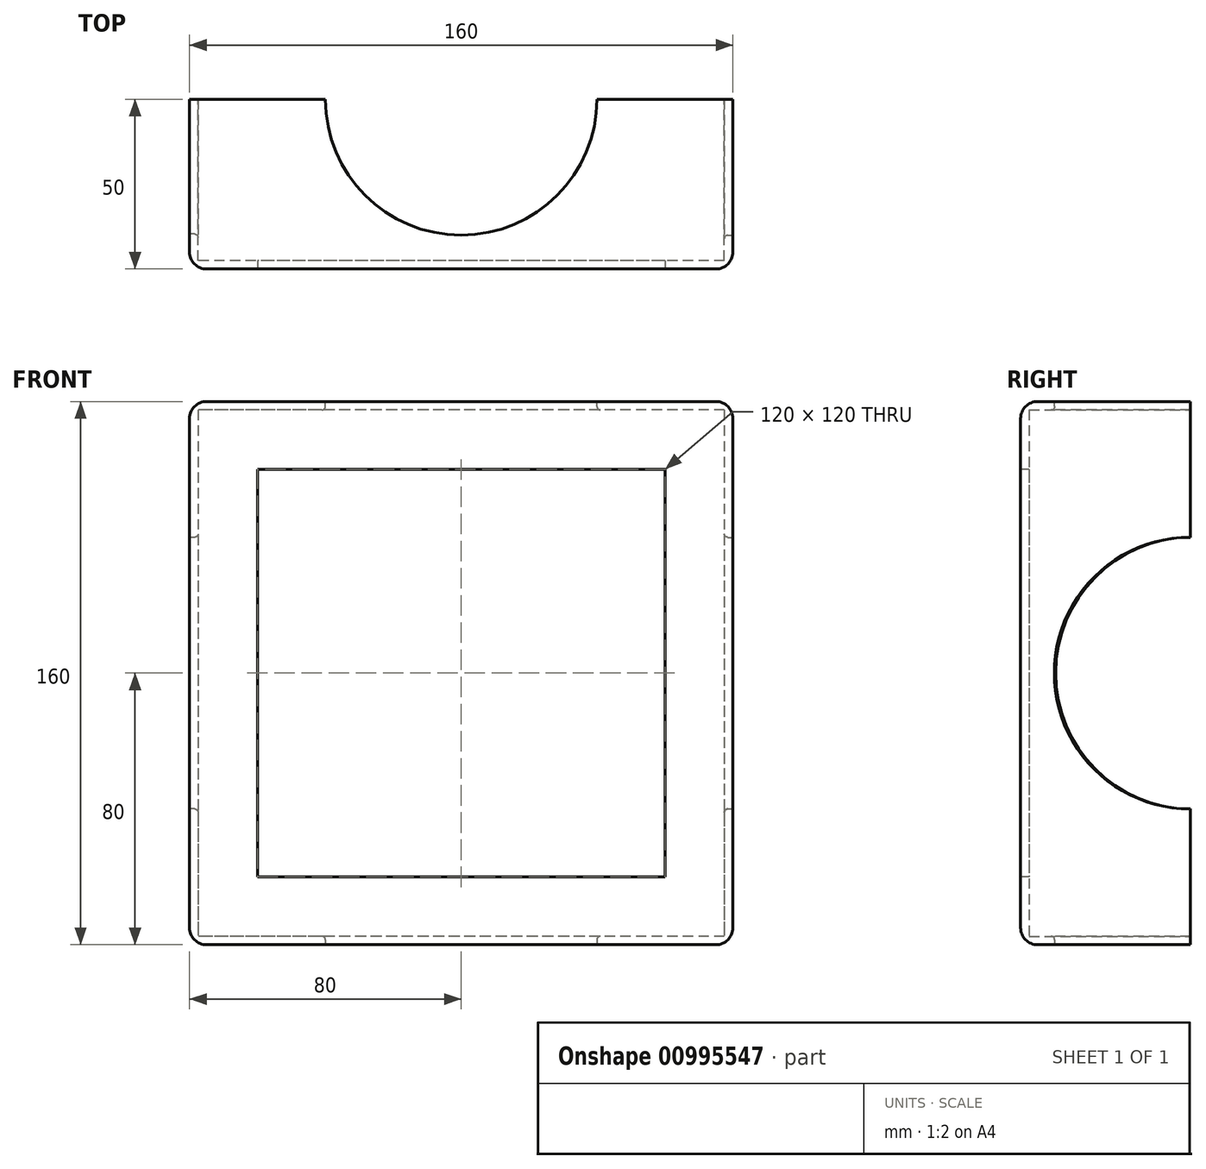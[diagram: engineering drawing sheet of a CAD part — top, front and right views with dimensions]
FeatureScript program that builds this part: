
annotation { "Feature Type Name" : "Feature", "Feature Type Description" : "" }
export const myFeature = defineFeature(function(context is Context, id is Id, definition is map)
    precondition{}
    {
        {
            var Q0;
            Q0=qCreatedBy(makeId("Front.planeOp"),FACE);
            var sketch = newSketch(context, id + "F0", { "sketchPlane" : qUnion([Q0])});
            skLineSegment(sketch, "E0.bottom", {"start": v(80, 80) * mm, "end": v(-80, 80) * mm});
            skLineSegment(sketch, "E0.top", {"start": v(80, -80) * mm, "end": v(-80, -80) * mm});
            skLineSegment(sketch, "E0.left", {"start": v(80, 80) * mm, "end": v(80, -80) * mm});
            skLineSegment(sketch, "E0.right", {"start": v(-80, 80) * mm, "end": v(-80, -80) * mm});
            skPoint(sketch, "E0.middle", {"position": v(0, 0) * mm});
            skSolve(sketch);
        }
        {
            var Q0;
            Q0 = qSketchRegion(id + "F0", true);
            extrude(context, id + "F1", {"entities" : qUnion([Q0]), "depth" : 50 * mm, "offsetDistance" : 25 * mm});
        }
        {
            var Q0;
            Q0=makeQuery(id+"F1.opExtrude","CAP_FACE",FACE,{"disambiguationData":[OSD([sQuery(id+"F0.wireOp",EDGE,"E0.bottom"),sQuery(id+"F0.wireOp",EDGE,"E0.top"),sQuery(id+"F0.wireOp",EDGE,"E0.left"),sQuery(id+"F0.wireOp",EDGE,"E0.right")])],"isStart":true});
            shell(context, id + "F2", {"entities" : qUnion([Q0]), "thickness" : 2.5 * mm});
        }
        {
            var Q0;
            Q0=makeQuery(id+"F1.opExtrude","SWEPT_FACE",FACE,{"disambiguationData":[OSD([sQuery(id+"F0.wireOp",EDGE,"E0.top")])]});
            var sketch = newSketch(context, id + "F3", { "sketchPlane" : qUnion([Q0])});
            skArc(sketch, "E1", {"start": v(40, 0) * mm, "mid": v(0, 40) * mm, "end": v(-40, 0) * mm});
            skSolve(sketch);
        }
        {
            var Q0;
            {var subQ0=sQuery(id+"F3.wireOp",EDGE,"E1");Q0=makeQuery(id+"F3.imprint","IMPRINT",FACE,{"disambiguationData":[TD([[makeQuery(id+"F3.imprint","IMPRINT",EDGE,{"derivedFrom":subQ0}),1.0]])]});}
            extrude(context, id + "F4", {"entities" : qUnion([Q0]), "operationType" : NewBodyOperationType.REMOVE, "oppositeDirection" : true, "depth" : 25 * mm, "offsetDistance" : 25 * mm});
        }
        {
            var Q0;
            Q0=makeQuery(id+"F1.opExtrude","SWEPT_FACE",FACE,{"disambiguationData":[OSD([sQuery(id+"F0.wireOp",EDGE,"E0.right")])]});
            var sketch = newSketch(context, id + "F5", { "sketchPlane" : qUnion([Q0])});
            skArc(sketch, "E2", {"start": v(0, -40) * mm, "mid": v(39.7, 0) * mm, "end": v(0, 40) * mm});
            skSolve(sketch);
        }
        {
            var Q0;
            {var subQ0=sQuery(id+"F5.wireOp",EDGE,"E2");Q0=makeQuery(id+"F5.imprint","IMPRINT",FACE,{"disambiguationData":[TD([[makeQuery(id+"F5.imprint","IMPRINT",EDGE,{"derivedFrom":subQ0}),1.0]])]});}
            extrude(context, id + "F6", {"entities" : qUnion([Q0]), "operationType" : NewBodyOperationType.REMOVE, "oppositeDirection" : true, "depth" : 25 * mm, "offsetDistance" : 25 * mm});
        }
        {
            var Q0;
            Q0=makeQuery(id+"F1.opExtrude","SWEPT_FACE",FACE,{"disambiguationData":[OSD([sQuery(id+"F0.wireOp",EDGE,"E0.bottom")])]});
            var sketch = newSketch(context, id + "F7", { "sketchPlane" : qUnion([Q0])});
            skArc(sketch, "E3", {"start": v(-40, 0) * mm, "mid": v(0, -40) * mm, "end": v(40, 0) * mm});
            skSolve(sketch);
        }
        {
            var Q0;
            {var subQ0=sQuery(id+"F7.wireOp",EDGE,"E3");Q0=makeQuery(id+"F7.imprint","IMPRINT",FACE,{"disambiguationData":[TD([[makeQuery(id+"F7.imprint","IMPRINT",EDGE,{"derivedFrom":subQ0}),1.0]])]});}
            extrude(context, id + "F8", {"entities" : qUnion([Q0]), "operationType" : NewBodyOperationType.REMOVE, "oppositeDirection" : true, "depth" : 25 * mm, "offsetDistance" : 25 * mm});
        }
        {
            var Q0;
            Q0=makeQuery(id+"F1.opExtrude","SWEPT_FACE",FACE,{"disambiguationData":[OSD([sQuery(id+"F0.wireOp",EDGE,"E0.left")])]});
            var sketch = newSketch(context, id + "F9", { "sketchPlane" : qUnion([Q0])});
            skArc(sketch, "E4", {"start": v(0, 40) * mm, "mid": v(-40.08, 0) * mm, "end": v(0, -40) * mm});
            skSolve(sketch);
        }
        {
            var Q0;
            {var subQ0=sQuery(id+"F9.wireOp",EDGE,"E4");Q0=makeQuery(id+"F9.imprint","IMPRINT",FACE,{"disambiguationData":[TD([[makeQuery(id+"F9.imprint","IMPRINT",EDGE,{"derivedFrom":subQ0}),1.0]])]});}
            extrude(context, id + "F10", {"entities" : qUnion([Q0]), "operationType" : NewBodyOperationType.REMOVE, "oppositeDirection" : true, "depth" : 25 * mm, "offsetDistance" : 25 * mm});
        }
        {
            var Q0;
            Q0=makeQuery(id+"F1.opExtrude","CAP_FACE",FACE,{"disambiguationData":[OSD([sQuery(id+"F0.wireOp",EDGE,"E0.bottom"),sQuery(id+"F0.wireOp",EDGE,"E0.top"),sQuery(id+"F0.wireOp",EDGE,"E0.left"),sQuery(id+"F0.wireOp",EDGE,"E0.right")])],"isStart":false});
            var sketch = newSketch(context, id + "F11", { "sketchPlane" : qUnion([Q0])});
            skLineSegment(sketch, "E5.bottom", {"start": v(60, 60) * mm, "end": v(-60, 60) * mm});
            skLineSegment(sketch, "E5.top", {"start": v(60, -60) * mm, "end": v(-60, -60) * mm});
            skLineSegment(sketch, "E5.left", {"start": v(60, 60) * mm, "end": v(60, -60) * mm});
            skLineSegment(sketch, "E5.right", {"start": v(-60, 60) * mm, "end": v(-60, -60) * mm});
            skPoint(sketch, "E5.middle", {"position": v(0, 0) * mm});
            skSolve(sketch);
        }
        {
            var Q0;
            Q0=makeQuery(id+"F11.imprint","IMPRINT",FACE,{"disambiguationData":[TD([[makeQuery(id+"F11.imprint","IMPRINT",EDGE,{"derivedFrom":sQuery(id+"F11.wireOp",EDGE,"E5.bottom")}),1.0]])]});
            extrude(context, id + "F12", {"entities" : qUnion([Q0]), "operationType" : NewBodyOperationType.REMOVE, "oppositeDirection" : true, "depth" : 25 * mm, "offsetDistance" : 25 * mm});
        }
        {
            var Q0;
            Q0=makeQuery(id+"F1.opExtrude","SWEPT_EDGE",EDGE,{"disambiguationData":[OSD([sQuery(id+"F0.wireOp",EDGE,"E0.bottom"),sQuery(id+"F0.wireOp",EDGE,"E0.left")])]});
            var Q1;
            Q1=makeQuery(id+"F1.opExtrude","CAP_EDGE",EDGE,{"disambiguationData":[OSD([sQuery(id+"F0.wireOp",EDGE,"E0.bottom")])],"isStart":false});
            var Q2;
            Q2=makeQuery(id+"F1.opExtrude","CAP_EDGE",EDGE,{"disambiguationData":[OSD([sQuery(id+"F0.wireOp",EDGE,"E0.left")])],"isStart":false});
            var Q3;
            Q3=makeQuery(id+"F1.opExtrude","SWEPT_EDGE",EDGE,{"disambiguationData":[OSD([sQuery(id+"F0.wireOp",EDGE,"E0.top"),sQuery(id+"F0.wireOp",EDGE,"E0.left")])]});
            var Q4;
            Q4=makeQuery(id+"F1.opExtrude","CAP_EDGE",EDGE,{"disambiguationData":[OSD([sQuery(id+"F0.wireOp",EDGE,"E0.top")])],"isStart":false});
            var Q5;
            Q5=makeQuery(id+"F1.opExtrude","SWEPT_EDGE",EDGE,{"disambiguationData":[OSD([sQuery(id+"F0.wireOp",EDGE,"E0.top"),sQuery(id+"F0.wireOp",EDGE,"E0.right")])]});
            var Q6;
            Q6=makeQuery(id+"F1.opExtrude","CAP_EDGE",EDGE,{"disambiguationData":[OSD([sQuery(id+"F0.wireOp",EDGE,"E0.right")])],"isStart":false});
            var Q7;
            Q7=makeQuery(id+"F1.opExtrude","SWEPT_EDGE",EDGE,{"disambiguationData":[OSD([sQuery(id+"F0.wireOp",EDGE,"E0.bottom"),sQuery(id+"F0.wireOp",EDGE,"E0.right")])]});
            fillet(context, id + "F13", {"entities" : qUnion([Q0, Q1, Q2, Q3, Q4, Q5, Q6, Q7]), "radius" : 5 * mm, "tangentPropagation" : true, "allowEdgeOverflow" : false});
        }
        {
            var Q0;
            Q0=makeQuery(id+"F4.boolean.opBoolean","INTERSECT",EDGE,{"derivedFrom":[makeQuery(id+"F2.opShell","OFFSET_FACE",FACE,{"disambiguationData":[OSD([sQuery(id+"F0.wireOp",EDGE,"E0.top")])]}),makeQuery(id+"F4.opExtrude","SWEPT_FACE",FACE,{"disambiguationData":[OSD([sQuery(id+"F3.wireOp",EDGE,"E1")])]})]});
            var Q1;
            Q1=makeQuery(id+"F4.boolean.opBoolean","COPY",EDGE,{"derivedFrom":makeQuery(id+"F4.opExtrude","CAP_EDGE",EDGE,{"disambiguationData":[OSD([sQuery(id+"F3.wireOp",EDGE,"E1")])],"isStart":true})});
            var Q2;
            Q2=makeQuery(id+"F10.boolean.opBoolean","INTERSECT",EDGE,{"derivedFrom":[makeQuery(id+"F2.opShell","OFFSET_FACE",FACE,{"disambiguationData":[OSD([sQuery(id+"F0.wireOp",EDGE,"E0.left")])]}),makeQuery(id+"F10.opExtrude","SWEPT_FACE",FACE,{"disambiguationData":[OSD([sQuery(id+"F9.wireOp",EDGE,"E4")])]})]});
            var Q3;
            Q3=makeQuery(id+"F10.boolean.opBoolean","COPY",EDGE,{"derivedFrom":makeQuery(id+"F10.opExtrude","CAP_EDGE",EDGE,{"disambiguationData":[OSD([sQuery(id+"F9.wireOp",EDGE,"E4")])],"isStart":true})});
            var Q4;
            Q4=makeQuery(id+"F8.boolean.opBoolean","INTERSECT",EDGE,{"derivedFrom":[makeQuery(id+"F2.opShell","OFFSET_FACE",FACE,{"disambiguationData":[OSD([sQuery(id+"F0.wireOp",EDGE,"E0.bottom")])]}),makeQuery(id+"F8.opExtrude","SWEPT_FACE",FACE,{"disambiguationData":[OSD([sQuery(id+"F7.wireOp",EDGE,"E3")])]})]});
            var Q5;
            Q5=makeQuery(id+"F8.boolean.opBoolean","COPY",EDGE,{"derivedFrom":makeQuery(id+"F8.opExtrude","CAP_EDGE",EDGE,{"disambiguationData":[OSD([sQuery(id+"F7.wireOp",EDGE,"E3")])],"isStart":true})});
            var Q6;
            Q6=makeQuery(id+"F6.boolean.opBoolean","INTERSECT",EDGE,{"derivedFrom":[makeQuery(id+"F2.opShell","OFFSET_FACE",FACE,{"disambiguationData":[OSD([sQuery(id+"F0.wireOp",EDGE,"E0.right")])]}),makeQuery(id+"F6.opExtrude","SWEPT_FACE",FACE,{"disambiguationData":[OSD([sQuery(id+"F5.wireOp",EDGE,"E2")])]})]});
            var Q7;
            Q7=makeQuery(id+"F6.boolean.opBoolean","COPY",EDGE,{"derivedFrom":makeQuery(id+"F6.opExtrude","CAP_EDGE",EDGE,{"disambiguationData":[OSD([sQuery(id+"F5.wireOp",EDGE,"E2")])],"isStart":true})});
            fillet(context, id + "F14", {"entities" : qUnion([Q0, Q1, Q2, Q3, Q4, Q5, Q6, Q7]), "radius" : 1 * mm, "tangentPropagation" : true, "allowEdgeOverflow" : false});
        }
    });
